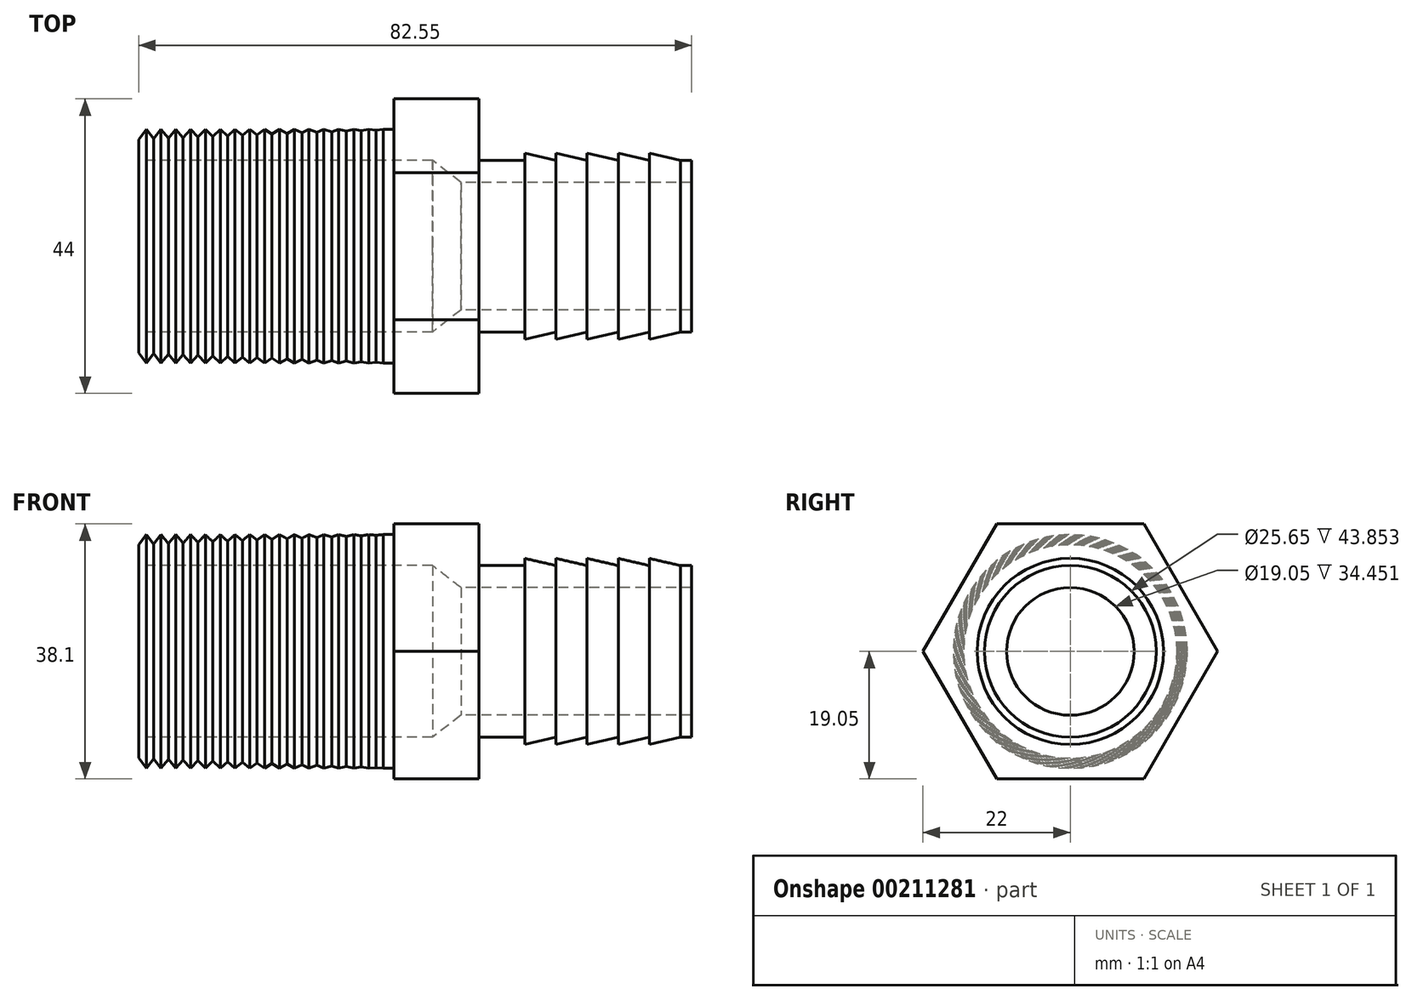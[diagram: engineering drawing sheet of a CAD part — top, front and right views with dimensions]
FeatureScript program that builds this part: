
annotation { "Feature Type Name" : "Feature", "Feature Type Description" : "" }
export const myFeature = defineFeature(function(context is Context, id is Id, definition is map)
    precondition{}
    {
        {
            var Q0;
            Q0=qCreatedBy(makeId("Front.planeOp"),FACE);
            var sketch = newSketch(context, id + "F0", { "sketchPlane" : qUnion([Q0])});
            skPoint(sketch, "E0.middle", {"position": v(0, 0) * mm});
            skLineSegment(sketch, "E1", {"start": v(31.75, 12.83) * mm, "end": v(30.09, 12.83) * mm});
            skLineSegment(sketch, "E2", {"start": v(30.09, 12.83) * mm, "end": v(25.44, 13.9) * mm});
            skLineSegment(sketch, "E3", {"start": v(25.44, 13.9) * mm, "end": v(25.44, 12.83) * mm});
            skLineSegment(sketch, "E4", {"start": v(6.85, 12.83) * mm, "end": v(6.85, 13.9) * mm});
            skLineSegment(sketch, "E5", {"start": v(6.85, 13.9) * mm, "end": v(11.5, 12.83) * mm});
            skLineSegment(sketch, "E6", {"start": v(11.5, 13.9) * mm, "end": v(16.14, 12.83) * mm});
            skLineSegment(sketch, "E7", {"start": v(16.14, 13.9) * mm, "end": v(20.8, 12.83) * mm});
            skLineSegment(sketch, "E8", {"start": v(20.8, 12.83) * mm, "end": v(20.8, 13.9) * mm});
            skLineSegment(sketch, "E9", {"start": v(20.8, 13.9) * mm, "end": v(25.44, 12.83) * mm});
            skLineSegment(sketch, "E10", {"start": v(16.14, 12.83) * mm, "end": v(16.14, 13.9) * mm});
            skLineSegment(sketch, "E11", {"start": v(11.5, 12.83) * mm, "end": v(11.5, 13.9) * mm});
            skLineSegment(sketch, "E12", {"start": v(6.85, 12.83) * mm, "end": v(0, 12.83) * mm});
            skLineSegment(sketch, "E13", {"start": v(0, 19.05) * mm, "end": v(-12.7, 19.05) * mm});
            skLineSegment(sketch, "E14", {"start": v(-50.8, 15.94) * mm, "end": v(-49.7, 17.46) * mm});
            skLineSegment(sketch, "E15", {"start": v(-49.7, 17.46) * mm, "end": v(-48.6, 16.03) * mm});
            skLineSegment(sketch, "E16", {"start": v(-48.6, 16.03) * mm, "end": v(-47.49, 17.46) * mm});
            skLineSegment(sketch, "E17", {"start": v(-47.49, 17.46) * mm, "end": v(-46.38, 16.11) * mm});
            skLineSegment(sketch, "E18", {"start": v(-46.38, 16.11) * mm, "end": v(-45.28, 17.46) * mm});
            skLineSegment(sketch, "E19", {"start": v(-45.28, 17.46) * mm, "end": v(-44.17, 16.2) * mm});
            skLineSegment(sketch, "E20", {"start": v(-44.17, 16.2) * mm, "end": v(-43.07, 17.46) * mm});
            skLineSegment(sketch, "E21", {"start": v(-43.07, 17.46) * mm, "end": v(-41.96, 16.3) * mm});
            skLineSegment(sketch, "E22", {"start": v(-41.96, 16.3) * mm, "end": v(-40.86, 17.46) * mm});
            skLineSegment(sketch, "E23", {"start": v(-39.48, 16.9) * mm, "end": v(-39.47, 16.9) * mm});
            skLineSegment(sketch, "E24", {"start": v(-38.65, 17.46) * mm, "end": v(-37.55, 16.47) * mm});
            skLineSegment(sketch, "E25", {"start": v(-37.55, 16.47) * mm, "end": v(-36.44, 17.46) * mm});
            skLineSegment(sketch, "E26", {"start": v(-36.44, 17.46) * mm, "end": v(-35.34, 16.56) * mm});
            skLineSegment(sketch, "E27", {"start": v(-34.23, 17.46) * mm, "end": v(-33.13, 16.64) * mm});
            skLineSegment(sketch, "E28", {"start": v(-33.13, 16.64) * mm, "end": v(-32.02, 17.46) * mm});
            skLineSegment(sketch, "E29", {"start": v(-30.92, 16.73) * mm, "end": v(-29.8, 17.46) * mm});
            skPoint(sketch, "E30.orphan", {"position": v(-40.28, 16.36) * mm});
            skPoint(sketch, "E31.start.orphan", {"position": v(-39.76, 16.38) * mm});
            skLineSegment(sketch, "E32", {"start": v(-40.86, 17.46) * mm, "end": v(-39.76, 16.38) * mm});
            skLineSegment(sketch, "E33", {"start": v(-39.76, 16.38) * mm, "end": v(-38.65, 17.46) * mm});
            skLineSegment(sketch, "E34", {"start": v(-35.34, 16.56) * mm, "end": v(-34.23, 17.46) * mm});
            skLineSegment(sketch, "E35", {"start": v(-32.02, 17.46) * mm, "end": v(-30.92, 16.73) * mm});
            skLineSegment(sketch, "E36", {"start": v(-29.8, 17.46) * mm, "end": v(-28.63, 16.82) * mm});
            skLineSegment(sketch, "E37", {"start": v(-28.63, 16.82) * mm, "end": v(-27.6, 17.46) * mm});
            skLineSegment(sketch, "E38", {"start": v(-27.6, 17.46) * mm, "end": v(-26.42, 16.91) * mm});
            skLineSegment(sketch, "E39", {"start": v(-26.42, 16.91) * mm, "end": v(-25.39, 17.46) * mm});
            skLineSegment(sketch, "E40", {"start": v(-25.39, 17.46) * mm, "end": v(-24.21, 17) * mm});
            skLineSegment(sketch, "E41", {"start": v(-24.21, 17) * mm, "end": v(-23.18, 17.46) * mm});
            skLineSegment(sketch, "E42", {"start": v(-23.18, 17.46) * mm, "end": v(-22, 17.1) * mm});
            skPoint(sketch, "E42.endSnap0", {"position": v(-22, 17.1) * mm});
            skLineSegment(sketch, "E43", {"start": v(-22, 17.1) * mm, "end": v(-20.97, 17.46) * mm});
            skLineSegment(sketch, "E44", {"start": v(-20.97, 17.46) * mm, "end": v(-19.8, 17.18) * mm});
            skLineSegment(sketch, "E45", {"start": v(-19.8, 17.18) * mm, "end": v(-18.69, 17.46) * mm});
            skLineSegment(sketch, "E46", {"start": v(-18.69, 17.46) * mm, "end": v(-17.58, 17.27) * mm});
            skLineSegment(sketch, "E47", {"start": v(-17.58, 17.27) * mm, "end": v(-16.48, 17.46) * mm});
            skLineSegment(sketch, "E48", {"start": v(-16.48, 17.46) * mm, "end": v(-15.38, 17.36) * mm});
            skLineSegment(sketch, "E49", {"start": v(-15.38, 17.36) * mm, "end": v(-14.27, 17.46) * mm});
            skLineSegment(sketch, "E50", {"start": v(-14.27, 17.46) * mm, "end": v(-12.7, 17.46) * mm});
            skLineSegment(sketch, "E51", {"start": v(-50.8, 15.94) * mm, "end": v(-50.8, 13.9) * mm});
            skLineSegment(sketch, "E52", {"start": v(0, 9.53) * mm, "end": v(31.75, 9.53) * mm});
            skLineSegment(sketch, "E53", {"start": v(31.75, 9.53) * mm, "end": v(31.75, 12.83) * mm});
            skLineSegment(sketch, "E54", {"start": v(-50.8, 15.94) * mm, "end": v(-50.8, 12.83) * mm});
            skLineSegment(sketch, "E55", {"start": v(-50.8, 12.83) * mm, "end": v(-6.95, 12.83) * mm});
            skLineSegment(sketch, "E56", {"start": v(-6.95, 12.83) * mm, "end": v(-2.7, 9.53) * mm});
            skLineSegment(sketch, "E57", {"start": v(-2.7, 9.53) * mm, "end": v(31.75, 9.53) * mm});
            skLineSegment(sketch, "E58", {"start": v(-12.7, 19.05) * mm, "end": v(-12.7, 17.46) * mm});
            skLineSegment(sketch, "E59", {"start": v(0, 12.83) * mm, "end": v(0, 19.05) * mm});
            skLineSegment(sketch, "E60", {"start": v(-46.97, 0) * mm, "end": v(-24.55, 0) * mm});
            skSolve(sketch);
        }
        {
            var Q0;
            Q0 = qSketchRegion(id + "F0", true);
            var Q1;
            Q1=sQuery(id+"F0.wireOp",EDGE,"E60");
            revolve(context, id + "F1", {"entities" : qUnion([Q0]), "axis" : qUnion([Q1]), "revolveType" : RevolveType.FULL});
        }
        {
            var Q0;
            Q0=makeQuery(id+"F1.opRevolve","SWEPT_FACE",FACE,{"disambiguationData":[OSD([sQuery(id+"F0.wireOp",EDGE,"E59")])]});
            var sketch = newSketch(context, id + "F2", { "sketchPlane" : qUnion([Q0])});
            skCircle(sketch, "E61.cCircle", {"center": v(0, 0) * mm, "radius": 19.05 * mm, "construction": true});
            skLineSegment(sketch, "E61.0", {"start": v(-11, 19.05) * mm, "end": v(11, 19.05) * mm});
            skLineSegment(sketch, "E61.1", {"start": v(11, 19.05) * mm, "end": v(22, 0) * mm});
            skLineSegment(sketch, "E61.2", {"start": v(22, 0) * mm, "end": v(11, -19.05) * mm});
            skLineSegment(sketch, "E61.3", {"start": v(11, -19.05) * mm, "end": v(-11, -19.05) * mm});
            skLineSegment(sketch, "E61.4", {"start": v(-11, -19.05) * mm, "end": v(-22, 0) * mm});
            skLineSegment(sketch, "E61.5", {"start": v(-22, 0) * mm, "end": v(-11, 19.05) * mm});
            skPoint(sketch, "E61.0.midPoint", {"position": v(0, 19.05) * mm});
            skCircle(sketch, "E62", {"center": v(0, 0) * mm, "radius": 13.99 * mm});
            skSolve(sketch);
        }
        {
            var Q0;
            Q0 = qSketchRegion(id + "F2", true);
            extrude(context, id + "F3", {"entities" : qUnion([Q0]), "operationType" : NewBodyOperationType.ADD, "oppositeDirection" : true, "depth" : 12.7 * mm});
        }
    });
